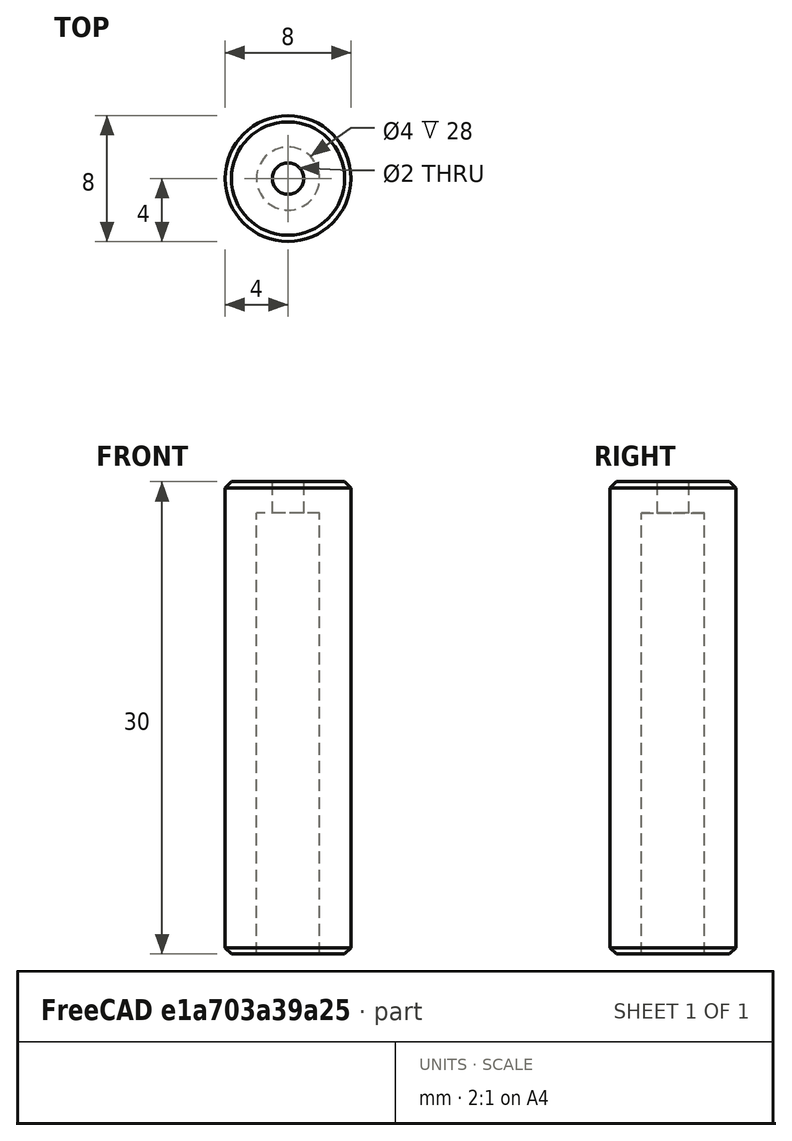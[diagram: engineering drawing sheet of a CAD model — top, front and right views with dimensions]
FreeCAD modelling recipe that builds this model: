
FCSTD DOCUMENT  (FreeCAD 0.18R16146 (Git))
Label: probe-temp-sensor-mount
License: All rights reserved
LicenseURL: http://en.wikipedia.org/wiki/All_rights_reserved
objects: Part::Cylinder×3, Part::MultiFuse×1, Part::Cut×1, Part::Chamfer×1
note: 6 computed .brp shape members not serialized (recipe doc carries the construction recipe); baked Part::Feature solids carry a one-line shape summary decoded from their .brp

FEATURE [Part::Cylinder] Cylinder
  Angle = 360
  AttacherType = Attacher::AttachEngine3D
  Height = 30
  Radius = 4
FEATURE [Part::Cylinder] Cylinder001
  Angle = 360
  AttacherType = Attacher::AttachEngine3D
  Height = 28
  Radius = 2
FEATURE [Part::Cylinder] Cylinder003
  Angle = 360
  AttacherType = Attacher::AttachEngine3D
  Height = 30
  Radius = 1
FEATURE [Part::MultiFuse] Fusion
  Shapes = -> [Cylinder001,Cylinder003]
FEATURE [Part::Cut] Cut
  Base = -> Cylinder
  Tool = -> Fusion
FEATURE [Part::Chamfer] Chamfer
  Base = -> Cut
  Edges = 2 edges r=0.4: [Edge1,Edge3]
